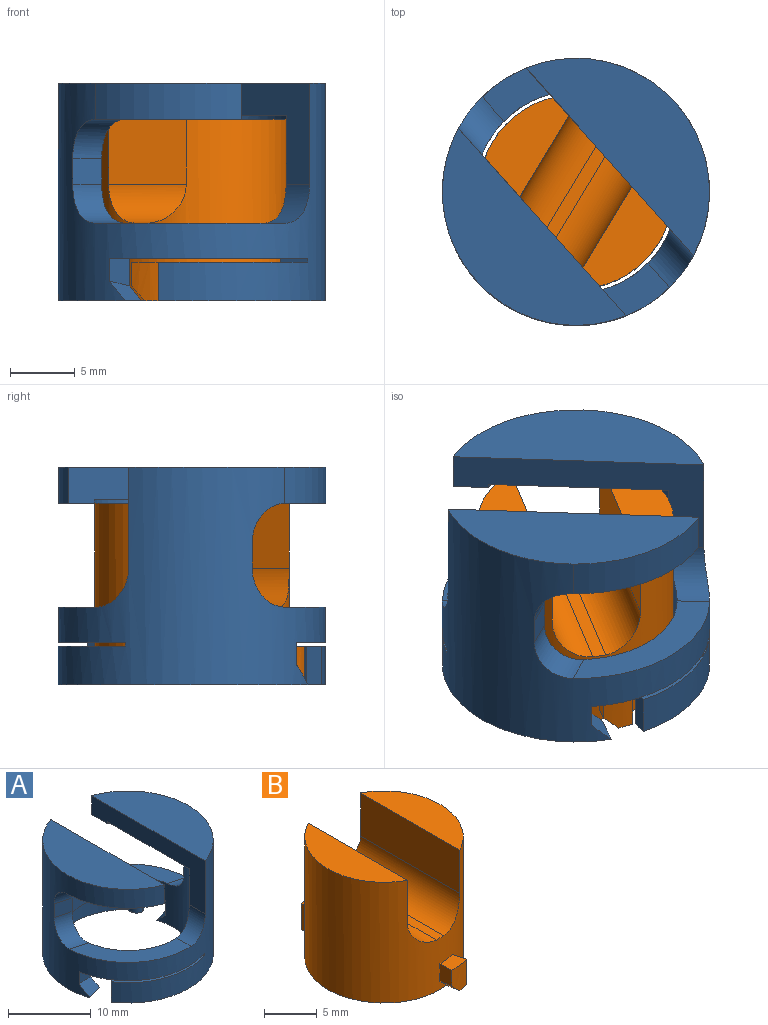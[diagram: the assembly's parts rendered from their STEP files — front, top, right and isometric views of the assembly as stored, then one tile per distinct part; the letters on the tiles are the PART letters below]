
ASSEMBLY  parts=2 mates=1
PART A: 44 faces, bbox 21.5x20.6x16.8 mm
  f0: cylinder r=7.8mm len=5.94mm, axis (0,0,1), area 2.3mm2, adj f1,f6,f8,f20
  f1: cylinder r=7.8mm len=15.6mm, axis (0,0,1), area 331.4mm2, adj f0,f2,f3,f6,f7,f8,f11,f12
  f2: plane 18.89x13.57mm, normal (0,0,-1), area 49.3mm2, adj f1,f4,f33,f36,f37,f38,f39,f43
  f3: plane 18.89x13.57mm, normal (0,0,-1), area 49.3mm2, adj f1,f4,f24,f27,f28,f29,f30,f42
  f4: cylinder r=10.3mm len=20.6mm, axis (0,0,1), area 631.9mm2, adj f2,f3,f5,f6,f7,f9,f10,f12
  f5: cylinder r=10.3mm len=9.34mm, axis (0,0,1), area 34.3mm2, adj f4,f6,f9,f20
  f6: plane 19.37x7.8mm, normal (-1,0,0), area 63.6mm2, adj f0,f1,f4,f5,f8,f9,f15,f20
  f7: plane 19.37x7.8mm, normal (1,0,0), area 63.6mm2, adj f1,f4,f10,f11,f12,f16
  f8: plane 13.94x4.3mm, normal (0,0,-1), area 42.9mm2, adj f0,f1,f6
  f9: plane 19.37x6.8mm, normal (0,0,1), area 96mm2, adj f4,f5,f6
  f10: plane 19.37x6.8mm, normal (0,0,1), area 96mm2, adj f4,f7
  f11: plane 13.94x4.3mm, normal (0,0,-1), area 42.9mm2, adj f1,f7
  f12: cylinder r=3mm len=3.32mm, axis (0,1,0), area 12.3mm2, adj f1,f4,f7,f13
  f13: plane 10.79x9.95mm, normal (0,0,1), area 35.1mm2, adj f1,f4,f12,f23
  f14: plane 10.79x9.95mm, normal (0,0,1), area 35.1mm2, adj f1,f4,f15,f19
  f15: cylinder r=3mm len=3.32mm, axis (0,1,0), area 12.3mm2, adj f1,f4,f6,f14
  f16: plane 9.34x6.79mm, normal (0,0,-1), area 24.8mm2, adj f1,f4,f7,f18
  f17: plane 2.42x2mm, normal (-0.26,-0.97,0), area 5mm2, adj f1,f4,f18,f19
  f18: cylinder r=3mm len=3.77mm, axis (0.97,-0.26,0), area 11.9mm2, adj f1,f4,f16,f17
  f19: cylinder r=3mm len=3.77mm, axis (-0.97,0.26,0), area 11.9mm2, adj f1,f4,f14,f17
  f20: plane 9.34x6.79mm, normal (0,0,-1), area 24.8mm2, adj f0,f5,f6,f22
  f21: plane 2.42x2mm, normal (0.26,0.97,0), area 5mm2, adj f1,f4,f22,f23
  f22: cylinder r=3mm len=3.77mm, axis (-0.97,0.26,0), area 11.9mm2, adj f1,f4,f20,f21
  f23: cylinder r=3mm len=3.77mm, axis (0.97,-0.26,0), area 11.9mm2, adj f1,f4,f13,f21
  f24: plane 3.3x2.42mm, normal (-0.97,-0.26,0), area 5.3mm2, adj f1,f3,f4,f26,f30,f31
  f25: plane 2.46x2.15mm, normal (0.17,-0.98,0), area 4.9mm2, adj f1,f4,f26,f32,f43
  f26: plane 13.38x8.95mm, normal (0,0,-1), area 39mm2, adj f1,f4,f24,f25
  f27: plane 3x1mm, normal (-0.55,0.83,0), area 3.6mm2, adj f3,f4,f28,f31
  f28: cylinder r=1mm len=3mm, axis (0,0,-1), area 6mm2, adj f3,f27,f29,f31
  f29: cylinder r=0.5mm len=3mm, axis (0,0,-1), area 1.7mm2, adj f3,f28,f30,f31
  f30: cylinder r=9.3mm len=9.32mm, axis (0,0,-1), area 30mm2, adj f3,f24,f29,f31
  f31: plane 11.83x5.28mm, normal (0,0,1), area 13.8mm2, adj f4,f24,f27,f28,f29,f30
  f32: plane 0.15x0.05mm, normal (0,0,1), area 0mm2, adj f4,f25,f43
  f33: plane 3.3x2.42mm, normal (0.97,0.26,0), area 5.3mm2, adj f1,f2,f4,f35,f39,f40
  f34: plane 2.46x2.15mm, normal (-0.17,0.98,0), area 4.9mm2, adj f1,f4,f35,f41,f42
  f35: plane 13.38x8.95mm, normal (0,0,-1), area 39mm2, adj f1,f4,f33,f34
  f36: plane 3x1mm, normal (0.55,-0.83,0), area 3.6mm2, adj f2,f4,f37,f40
  f37: cylinder r=1mm len=3mm, axis (0,0,-1), area 6mm2, adj f2,f36,f38,f40
  f38: cylinder r=0.5mm len=3mm, axis (0,0,-1), area 1.7mm2, adj f2,f37,f39,f40
  f39: cylinder r=9.3mm len=9.32mm, axis (0,0,-1), area 30mm2, adj f2,f33,f38,f40
  f40: plane 11.83x5.28mm, normal (0,0,1), area 13.8mm2, adj f4,f33,f36,f37,f38,f39
  f41: plane 0.15x0.05mm, normal (0,0,1), area 0mm2, adj f4,f34,f42
  f42: plane 2.75x1.92mm, normal (-0.22,0.67,0.71), area 4.7mm2, adj f1,f3,f4,f34,f41
  f43: plane 2.75x1.92mm, normal (0.22,-0.67,0.71), area 4.7mm2, adj f1,f2,f4,f25,f32
PART B: 19 faces, bbox 15x18.1x14 mm
  f0: cylinder r=7.5mm len=15mm, axis (0,0,1), area 540.8mm2, adj f1,f2,f3,f4,f5,f6,f7,f8
  f1: plane 13.27x4mm, normal (0,0,1), area 37.8mm2, adj f0,f6
  f2: plane 13.27x4mm, normal (0,0,1), area 37.8mm2, adj f0,f7
  f3: plane 17.95x15mm, normal (0,0,-1), area 180.1mm2, adj f0,f9,f11,f13,f15,f17,f18
  f4: plane 15x1mm, normal (0,0,1), area 15mm2, adj f0,f5,f8
  f5: cylinder r=3mm len=14.97mm, axis (0,1,0), area 66.3mm2, adj f0,f4,f6
  f6: plane 13.27x5mm, normal (-1,0,0), area 66.3mm2, adj f0,f1,f5
  f7: plane 13.27x5mm, normal (1,0,0), area 66.3mm2, adj f0,f2,f8
  f8: cylinder r=3mm len=14.97mm, axis (0,1,0), area 66.3mm2, adj f0,f4,f7
  f9: cylinder r=9.05mm len=3mm, axis (0,0,-1), area 6.4mm2, adj f3,f10,f11,f12,f17
  f10: plane 2.02x1.55mm, normal (-1,0,0), area 3mm2, adj f0,f9,f12,f17
  f11: plane 3x1.5mm, normal (0.97,0.26,0), area 4.6mm2, adj f0,f3,f9,f12
  f12: plane 2.34x1.81mm, normal (0,0,1), area 3.4mm2, adj f0,f9,f10,f11
  f13: cylinder r=9.05mm len=3mm, axis (0,0,-1), area 6.4mm2, adj f3,f14,f15,f16,f18
  f14: plane 2.02x1.55mm, normal (1,0,0), area 3mm2, adj f0,f13,f16,f18
  f15: plane 3x1.5mm, normal (-0.97,-0.26,0), area 4.6mm2, adj f0,f3,f13,f16
  f16: plane 2.34x1.81mm, normal (0,0,1), area 3.4mm2, adj f0,f13,f14,f15
  f17: plane 1.62x1.18mm, normal (-0.7,-0.09,-0.71), area 2.4mm2, adj f0,f3,f9,f10
  f18: plane 1.62x1.18mm, normal (0.7,0.09,-0.71), area 2.4mm2, adj f0,f3,f13,f14
PLACE A rot(axis=(0,0,-1),138.2deg) t=(7.77,1.58,-0.95)mm
PLACE B rot(axis=(0,0,1),148.8deg) t=(7.77,1.58,-0.95)mm
MATE revolute B.f0 <-> A.f0  axis (0,0,-1) through (7.77,1.58,-0.95)mm
